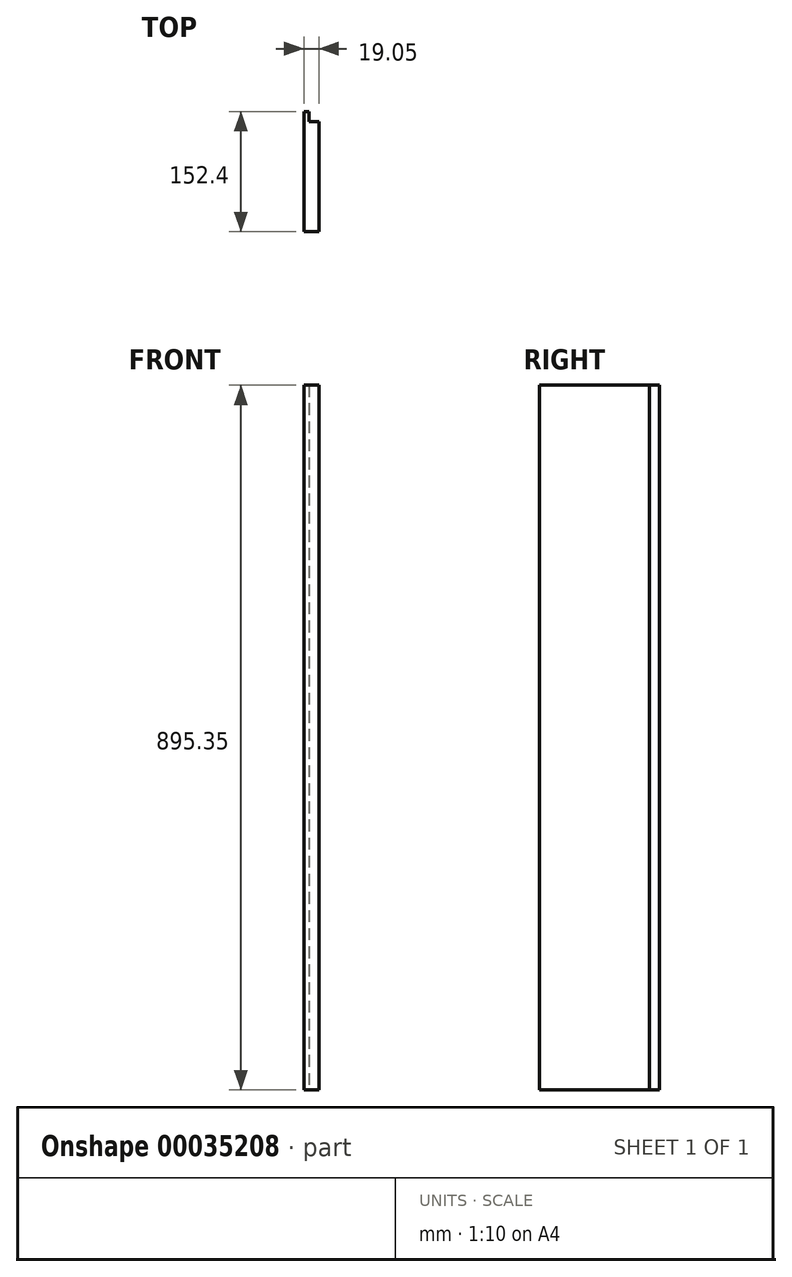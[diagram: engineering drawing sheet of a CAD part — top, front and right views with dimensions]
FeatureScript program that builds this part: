
annotation { "Feature Type Name" : "Feature", "Feature Type Description" : "" }
export const myFeature = defineFeature(function(context is Context, id is Id, definition is map)
    precondition{}
    {
        {
            var Q0;
            Q0=qCreatedBy(makeId("Right.planeOp"),FACE);
            var sketch = newSketch(context, id + "F0", { "sketchPlane" : qUnion([Q0])});
            skLineSegment(sketch, "E0.bottom", {"start": v(0, 0) * mm, "end": v(-152.4, 0) * mm});
            skLineSegment(sketch, "E0.top", {"start": v(0, 895.35) * mm, "end": v(-152.4, 895.35) * mm});
            skLineSegment(sketch, "E0.left", {"start": v(0, 0) * mm, "end": v(0, 895.35) * mm});
            skLineSegment(sketch, "E0.right", {"start": v(-152.4, 0) * mm, "end": v(-152.4, 895.35) * mm});
            skSolve(sketch);
        }
        {
            var Q0;
            Q0=makeQuery(id+"F0.imprint","IMPRINT",FACE,{"disambiguationData":[TD([[makeQuery(id+"F0.imprint","IMPRINT",EDGE,{"derivedFrom":sQuery(id+"F0.wireOp",EDGE,"E0.bottom")}),-1.0]])]});
            extrude(context, id + "F1", {"entities" : qUnion([Q0]), "depth" : 19.05 * mm});
        }
        {
            var Q0;
            Q0=qCreatedBy(makeId("Top.planeOp"),FACE);
            var sketch = newSketch(context, id + "F2", { "sketchPlane" : qUnion([Q0])});
            skLineSegment(sketch, "E1", {"start": v(6.35, 0) * mm, "end": v(6.35, -12.7) * mm});
            skLineSegment(sketch, "E2", {"start": v(6.35, -12.7) * mm, "end": v(19.05, -12.7) * mm});
            skLineSegment(sketch, "E3", {"start": v(19.05, -12.7) * mm, "end": v(19.05, 0) * mm});
            skLineSegment(sketch, "E4", {"start": v(19.05, 0) * mm, "end": v(6.35, 0) * mm});
            skSolve(sketch);
        }
        {
            var Q0;
            Q0=makeQuery(id+"F2.imprint","IMPRINT",FACE,{"disambiguationData":[TD([[makeQuery(id+"F2.imprint","IMPRINT",EDGE,{"derivedFrom":sQuery(id+"F2.wireOp",EDGE,"E1")}),1.0]])]});
            extrude(context, id + "F3", {"entities" : qUnion([Q0]), "operationType" : NewBodyOperationType.REMOVE, "endBound" : BoundingType.THROUGH_ALL, "depth" : 25.4 * mm});
        }
    });
